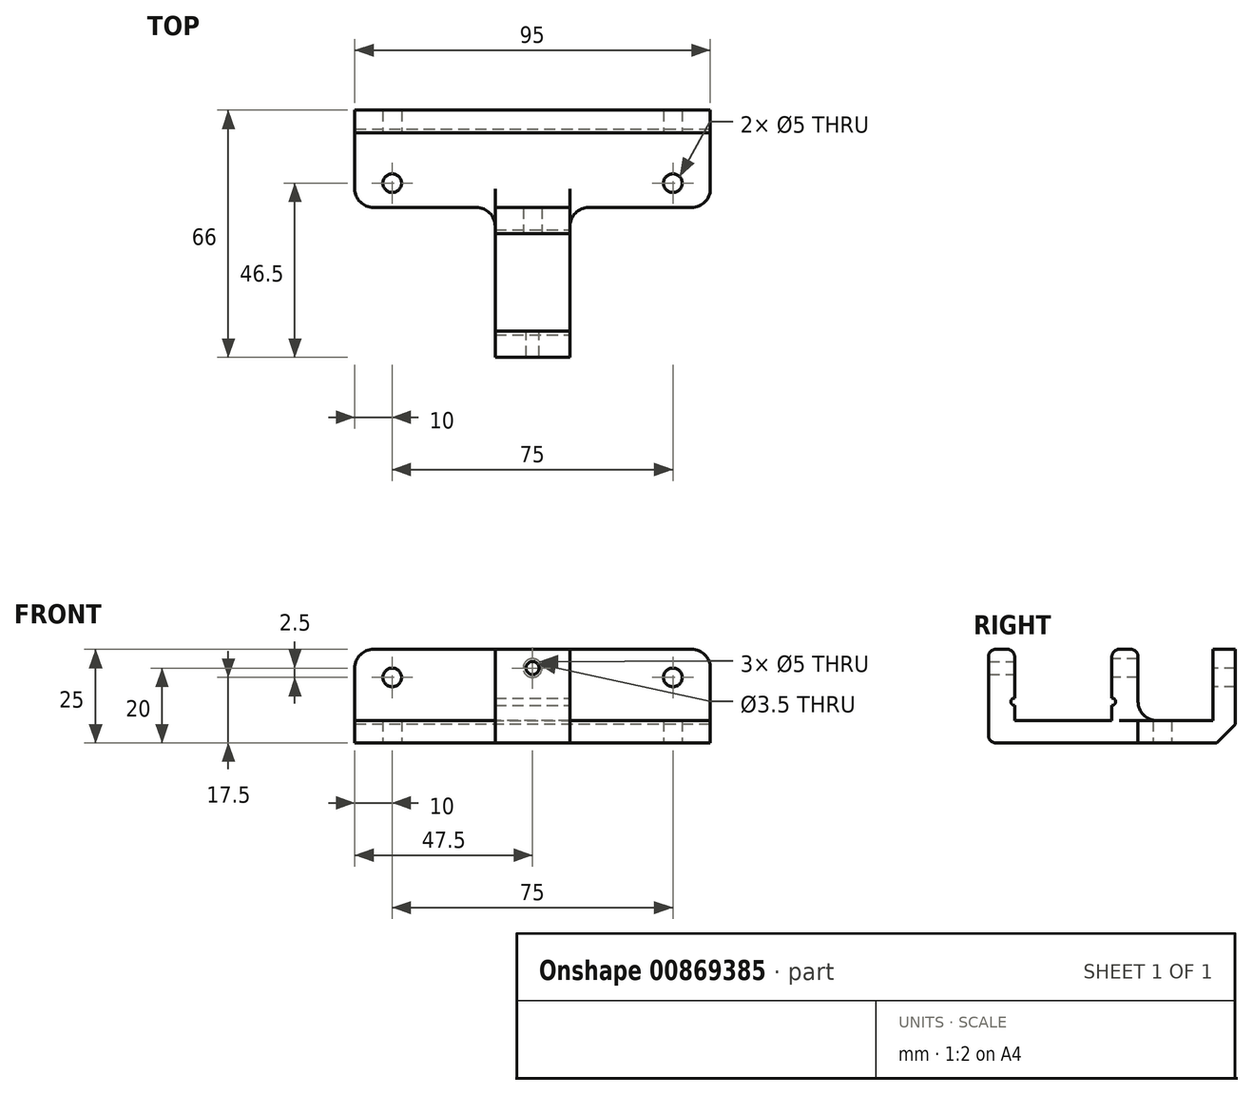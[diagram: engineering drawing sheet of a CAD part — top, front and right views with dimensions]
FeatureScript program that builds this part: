
annotation { "Feature Type Name" : "Feature", "Feature Type Description" : "" }
export const myFeature = defineFeature(function(context is Context, id is Id, definition is map)
    precondition{}
    {
        {
            var Q0;
            Q0=qCreatedBy(makeId("Top.planeOp"),FACE);
            var sketch = newSketch(context, id + "F0", { "sketchPlane" : qUnion([Q0])});
            skCircle(sketch, "E0", {"center": v(-37.5, 6.5) * mm, "radius": 2.5 * mm});
            skCircle(sketch, "E1", {"center": v(37.5, 6.5) * mm, "radius": 2.5 * mm});
            skLineSegment(sketch, "E2.bottom", {"start": v(-47.5, 0) * mm, "end": v(47.5, 0) * mm});
            skLineSegment(sketch, "E2.top", {"start": v(-47.5, 20) * mm, "end": v(47.5, 20) * mm});
            skLineSegment(sketch, "E2.left", {"start": v(-47.5, 0) * mm, "end": v(-47.5, 20) * mm});
            skLineSegment(sketch, "E2.right", {"start": v(47.5, 0) * mm, "end": v(47.5, 20) * mm});
            skLineSegment(sketch, "E3.top", {"start": v(-47.5, 26) * mm, "end": v(47.5, 26) * mm});
            skLineSegment(sketch, "E3.left", {"start": v(-47.5, 20) * mm, "end": v(-47.5, 26) * mm});
            skLineSegment(sketch, "E3.right", {"start": v(47.5, 20) * mm, "end": v(47.5, 26) * mm});
            skLineSegment(sketch, "E4.bottom", {"start": v(-10, 0) * mm, "end": v(10, 0) * mm});
            skLineSegment(sketch, "E4.top", {"start": v(-10, -40) * mm, "end": v(10, -40) * mm});
            skLineSegment(sketch, "E4.left", {"start": v(-10, 0) * mm, "end": v(-10, -40) * mm});
            skLineSegment(sketch, "E4.right", {"start": v(10, 0) * mm, "end": v(10, -40) * mm});
            skLineSegment(sketch, "E5.top", {"start": v(-10, -33) * mm, "end": v(10, -33) * mm});
            skLineSegment(sketch, "E5.left", {"start": v(-10, -40) * mm, "end": v(-10, -33) * mm});
            skLineSegment(sketch, "E5.right", {"start": v(10, -40) * mm, "end": v(10, -33) * mm});
            skLineSegment(sketch, "E6.top", {"start": v(-10, -7) * mm, "end": v(10, -7) * mm});
            skLineSegment(sketch, "E6.left", {"start": v(-10, 0) * mm, "end": v(-10, -7) * mm});
            skLineSegment(sketch, "E6.right", {"start": v(10, 0) * mm, "end": v(10, -7) * mm});
            skSolve(sketch);
        }
        {
            var Q0;
            Q0=makeQuery(id+"F0.imprint","IMPRINT",FACE,{"disambiguationData":[TD([[makeQuery(id+"F0.imprint","IMPRINT",EDGE,{"derivedFrom":sQuery(id+"F0.wireOp",EDGE,"E0")}),-1.0]])]});
            var Q1;
            {var subQ2=sQuery(id+"F0.wireOp",EDGE,"E5.top");Q1=makeQuery(id+"F0.imprint","IMPRINT",FACE,{"disambiguationData":[TD([[makeQuery(id+"F0.imprint","IMPRINT",EDGE,{"derivedFrom":subQ2}),1.0]])]});}
            var Q2;
            {var subQ0=sQuery(id+"F0.wireOp",EDGE,"E4.top");Q2=makeQuery(id+"F0.imprint","IMPRINT",FACE,{"disambiguationData":[TD([[makeQuery(id+"F0.imprint","IMPRINT",EDGE,{"derivedFrom":subQ0}),1.0]])]});}
            var Q3;
            {var subQ5=sQuery(id+"F0.wireOp",EDGE,"E6.top");Q3=makeQuery(id+"F0.imprint","IMPRINT",FACE,{"disambiguationData":[TD([[makeQuery(id+"F0.imprint","IMPRINT",EDGE,{"derivedFrom":subQ5}),1.0]])]});}
            extrude(context, id + "F1", {"entities" : qUnion([Q0, Q1, Q2, Q3]), "depth" : 6 * mm, "offsetDistance" : 25 * mm});
        }
        {
            var Q0;
            Q0=makeQuery(id+"F0.imprint","IMPRINT",FACE,{"disambiguationData":[TD([[makeQuery(id+"F0.imprint","IMPRINT",EDGE,{"derivedFrom":sQuery(id+"F0.wireOp",EDGE,"E2.top")}),1.0]])]});
            extrude(context, id + "F2", {"entities" : qUnion([Q0]), "operationType" : NewBodyOperationType.ADD, "depth" : 25 * mm, "offsetDistance" : 25 * mm});
        }
        {
            var Q0;
            Q0=makeQuery(id+"F2.opExtrude","SWEPT_FACE",FACE,{"disambiguationData":[OSD([sQuery(id+"F0.wireOp",EDGE,"E2.top")])]});
            var sketch = newSketch(context, id + "F3", { "sketchPlane" : qUnion([Q0])});
            skCircle(sketch, "E7", {"center": v(-37.5, 17.5) * mm, "radius": 2.5 * mm});
            skCircle(sketch, "E8", {"center": v(37.5, 17.5) * mm, "radius": 2.5 * mm});
            skSolve(sketch);
        }
        {
            var Q0;
            Q0=makeQuery(id+"F3.imprint","IMPRINT",FACE,{"disambiguationData":[TD([[makeQuery(id+"F3.imprint","IMPRINT",EDGE,{"derivedFrom":sQuery(id+"F3.wireOp",EDGE,"E7")}),1.0]])]});
            var Q1;
            Q1=makeQuery(id+"F3.imprint","IMPRINT",FACE,{"disambiguationData":[TD([[makeQuery(id+"F3.imprint","IMPRINT",EDGE,{"derivedFrom":sQuery(id+"F3.wireOp",EDGE,"E8")}),1.0]])]});
            extrude(context, id + "F4", {"entities" : qUnion([Q0, Q1]), "operationType" : NewBodyOperationType.REMOVE, "oppositeDirection" : true, "depth" : 25 * mm, "offsetDistance" : 25 * mm});
        }
        {
            var Q0;
            Q0=makeQuery(id+"F1.opExtrude","CAP_EDGE",EDGE,{"disambiguationData":[OSD([sQuery(id+"F0.wireOp",EDGE,"E2.top")])],"isStart":false});
            var Q1;
            Q1=makeQuery(id+"F2.opExtrude","CAP_EDGE",EDGE,{"disambiguationData":[OSD([sQuery(id+"F0.wireOp",EDGE,"E3.top")])],"isStart":true});
            chamfer(context, id + "F5", {"entities" : qUnion([Q0, Q1]), "width" : 5 * mm, "tangentPropagation" : true});
        }
        {
            var Q0;
            Q0=makeQuery(id+"F2.opExtrude","CAP_EDGE",EDGE,{"disambiguationData":[OSD([sQuery(id+"F0.wireOp",EDGE,"E3.right")])],"isStart":false});
            var Q1;
            Q1=makeQuery(id+"F1.opExtrude","SWEPT_EDGE",EDGE,{"disambiguationData":[OSD([sQuery(id+"F0.wireOp",EDGE,"E2.bottom"),sQuery(id+"F0.wireOp",EDGE,"E2.right")])]});
            var Q2;
            Q2=makeQuery(id+"F1.opExtrude","SWEPT_EDGE",EDGE,{"disambiguationData":[OSD([sQuery(id+"F0.wireOp",EDGE,"E2.bottom"),sQuery(id+"F0.wireOp",EDGE,"E2.left")])]});
            var Q3;
            Q3=makeQuery(id+"F2.opExtrude","CAP_EDGE",EDGE,{"disambiguationData":[OSD([sQuery(id+"F0.wireOp",EDGE,"E3.left")])],"isStart":false});
            fillet(context, id + "F6", {"entities" : qUnion([Q0, Q1, Q2, Q3]), "radius" : 5 * mm, "tangentPropagation" : true, "allowEdgeOverflow" : false});
        }
        {
            var Q0;
            {var subQ5=sQuery(id+"F0.wireOp",EDGE,"E6.top");Q0=makeQuery(id+"F0.imprint","IMPRINT",FACE,{"disambiguationData":[TD([[makeQuery(id+"F0.imprint","IMPRINT",EDGE,{"derivedFrom":subQ5}),1.0]])]});}
            var Q1;
            {var subQ0=sQuery(id+"F0.wireOp",EDGE,"E4.top");Q1=makeQuery(id+"F0.imprint","IMPRINT",FACE,{"disambiguationData":[TD([[makeQuery(id+"F0.imprint","IMPRINT",EDGE,{"derivedFrom":subQ0}),1.0]])]});}
            extrude(context, id + "F7", {"entities" : qUnion([Q0, Q1]), "operationType" : NewBodyOperationType.ADD, "depth" : 25 * mm, "offsetDistance" : 25 * mm});
        }
        {
            var Q0;
            {var subQ0=sQuery(id+"F0.wireOp",EDGE,"E4.right");Q0=makeQuery(id+"F7.boolean.opBoolean","MERGE",FACE,{"derivedFrom":[makeQuery(id+"F1.opExtrude","SWEPT_FACE",FACE,{"disambiguationData":[OSD([subQ0])]}),makeQuery(id+"F7.opExtrude","SWEPT_FACE",FACE,{"disambiguationData":[OSD([subQ0]),TDD([makeQuery(id+"F0.imprint","IMPRINT",EDGE,{"disambiguationData":[TD([[makeQuery(id+"F0.imprint","INTERSECT",VERTEX,{"derivedFrom":[sQuery(id+"F0.wireOp",EDGE,"E4.top"),subQ0]}),1.0]])],"derivedFrom":subQ0})])]}),makeQuery(id+"F7.opExtrude","SWEPT_FACE",FACE,{"disambiguationData":[OSD([subQ0]),TDD([makeQuery(id+"F0.imprint","IMPRINT",EDGE,{"disambiguationData":[TD([[makeQuery(id+"F0.imprint","INTERSECT",VERTEX,{"derivedFrom":[sQuery(id+"F0.wireOp",EDGE,"E2.bottom"),subQ0]}),-1.0]])],"derivedFrom":subQ0})])]})]});}
            var sketch = newSketch(context, id + "F8", { "sketchPlane" : qUnion([Q0])});
            skCircle(sketch, "E9", {"center": v(-33, 11) * mm, "radius": 1 * mm});
            skCircle(sketch, "E10", {"center": v(-7, 11) * mm, "radius": 1 * mm});
            skSolve(sketch);
        }
        {
            var Q0;
            {var subQ0=sQuery(id+"F8.wireOp",EDGE,"E9");var subQ1=makeQuery(id+"F7.opExtrude","SWEPT_EDGE",EDGE,{"disambiguationData":[OSD([sQuery(id+"F0.wireOp",EDGE,"E4.right"),sQuery(id+"F0.wireOp",EDGE,"E5.top")])]});var subQ2=makeQuery(id+"F8.imprint","INTERSECT",VERTEX,{"disambiguationData":[OD(0.0)],"derivedFrom":[subQ1,subQ0]});Q0=makeQuery(id+"F8.imprint","IMPRINT",FACE,{"disambiguationData":[TD([[makeQuery(id+"F8.imprint","IMPRINT",EDGE,{"disambiguationData":[TD([[subQ2,-1.0]])],"derivedFrom":subQ0}),1.0]])]});}
            var Q1;
            {var subQ0=sQuery(id+"F8.wireOp",EDGE,"E10");var subQ1=makeQuery(id+"F7.opExtrude","SWEPT_EDGE",EDGE,{"disambiguationData":[OSD([sQuery(id+"F0.wireOp",EDGE,"E4.right"),sQuery(id+"F0.wireOp",EDGE,"E6.top")])]});var subQ2=makeQuery(id+"F8.imprint","INTERSECT",VERTEX,{"disambiguationData":[OD(0.0)],"derivedFrom":[subQ1,subQ0]});Q1=makeQuery(id+"F8.imprint","IMPRINT",FACE,{"disambiguationData":[TD([[makeQuery(id+"F8.imprint","IMPRINT",EDGE,{"disambiguationData":[TD([[subQ2,1.0]])],"derivedFrom":subQ0}),1.0]])]});}
            extrude(context, id + "F9", {"entities" : qUnion([Q0, Q1]), "operationType" : NewBodyOperationType.REMOVE, "oppositeDirection" : true, "depth" : 25 * mm, "offsetDistance" : 25 * mm});
        }
        {
            var Q0;
            {var subQ0=sQuery(id+"F0.wireOp",EDGE,"E6.top");var subQ1=sQuery(id+"F0.wireOp",EDGE,"E4.right");var subQ2=sQuery(id+"F0.wireOp",EDGE,"E4.left");var subQ3=sQuery(id+"F0.wireOp",EDGE,"E2.bottom");Q0=makeQuery(id+"F9.boolean.opBoolean","SPLIT",FACE,{"disambiguationData":[TD([makeQuery(id+"F7.opExtrude","CAP_FACE",FACE,{"disambiguationData":[OSD([subQ3,subQ2,subQ1,subQ0])],"isStart":false})])],"derivedFrom":makeQuery(id+"F7.opExtrude","SWEPT_FACE",FACE,{"disambiguationData":[OSD([subQ0])]})});}
            var sketch = newSketch(context, id + "F10", { "sketchPlane" : qUnion([Q0])});
            skCircle(sketch, "E11", {"center": v(0, 20) * mm, "radius": 1.75 * mm});
            skPoint(sketch, "E11.centerSnap0", {"position": v(0, 25) * mm});
            skCircle(sketch, "E12", {"center": v(0, 20) * mm, "radius": 2.5 * mm});
            skSolve(sketch);
        }
        {
            var Q0;
            Q0=makeQuery(id+"F10.imprint","IMPRINT",FACE,{"disambiguationData":[TD([[makeQuery(id+"F10.imprint","IMPRINT",EDGE,{"derivedFrom":sQuery(id+"F10.wireOp",EDGE,"E11")}),1.0]])]});
            extrude(context, id + "F11", {"entities" : qUnion([Q0]), "operationType" : NewBodyOperationType.REMOVE, "depth" : 50 * mm, "offsetDistance" : 25 * mm});
        }
        {
            var Q0;
            Q0=makeQuery(id+"F10.imprint","IMPRINT",FACE,{"disambiguationData":[TD([[makeQuery(id+"F10.imprint","IMPRINT",EDGE,{"derivedFrom":sQuery(id+"F10.wireOp",EDGE,"E11")}),-1.0]])]});
            var Q1;
            Q1=makeQuery(id+"F10.imprint","IMPRINT",FACE,{"disambiguationData":[TD([[makeQuery(id+"F10.imprint","IMPRINT",EDGE,{"derivedFrom":sQuery(id+"F10.wireOp",EDGE,"E11")}),1.0]])]});
            extrude(context, id + "F12", {"entities" : qUnion([Q0, Q1]), "operationType" : NewBodyOperationType.REMOVE, "oppositeDirection" : true, "depth" : 10 * mm, "offsetDistance" : 25 * mm});
        }
        {
            var Q0;
            Q0=makeQuery(id+"F7.opExtrude","CAP_EDGE",EDGE,{"disambiguationData":[OSD([sQuery(id+"F0.wireOp",EDGE,"E6.top")])],"isStart":false});
            var Q1;
            Q1=makeQuery(id+"F7.opExtrude","CAP_EDGE",EDGE,{"disambiguationData":[OSD([sQuery(id+"F0.wireOp",EDGE,"E2.bottom")])],"isStart":false});
            var Q2;
            Q2=makeQuery(id+"F7.opExtrude","CAP_EDGE",EDGE,{"disambiguationData":[OSD([sQuery(id+"F0.wireOp",EDGE,"E5.top")])],"isStart":false});
            var Q3;
            Q3=makeQuery(id+"F7.opExtrude","CAP_EDGE",EDGE,{"disambiguationData":[OSD([sQuery(id+"F0.wireOp",EDGE,"E4.top")])],"isStart":false});
            var Q4;
            Q4=makeQuery(id+"F1.opExtrude","CAP_EDGE",EDGE,{"disambiguationData":[OSD([sQuery(id+"F0.wireOp",EDGE,"E4.top")])],"isStart":true});
            fillet(context, id + "F13", {"entities" : qUnion([Q0, Q1, Q2, Q3, Q4]), "radius" : 2 * mm, "tangentPropagation" : true, "allowEdgeOverflow" : false});
        }
        {
            var Q0;
            {var subQ0=sQuery(id+"F0.wireOp",EDGE,"E2.bottom");Q0=makeQuery(id+"F7.boolean.opBoolean","INTERSECT",EDGE,{"derivedFrom":[makeQuery(id+"F1.opExtrude","CAP_FACE",FACE,{"disambiguationData":[OSD([sQuery(id+"F0.wireOp",EDGE,"E0"),sQuery(id+"F0.wireOp",EDGE,"E1"),subQ0,sQuery(id+"F0.wireOp",EDGE,"E2.top"),sQuery(id+"F0.wireOp",EDGE,"E2.left"),sQuery(id+"F0.wireOp",EDGE,"E2.right"),sQuery(id+"F0.wireOp",EDGE,"E4.top"),sQuery(id+"F0.wireOp",EDGE,"E4.left"),sQuery(id+"F0.wireOp",EDGE,"E4.right")])],"isStart":false}),makeQuery(id+"F7.opExtrude","SWEPT_FACE",FACE,{"disambiguationData":[OSD([subQ0])]})]});}
            fillet(context, id + "F14", {"entities" : qUnion([Q0]), "radius" : 5 * mm, "tangentPropagation" : true, "allowEdgeOverflow" : false});
        }
        {
            var Q0;
            Q0=makeQuery(id+"F1.opExtrude","SWEPT_EDGE",EDGE,{"disambiguationData":[OSD([sQuery(id+"F0.wireOp",EDGE,"E2.bottom"),sQuery(id+"F0.wireOp",EDGE,"E4.right")])]});
            var Q1;
            Q1=makeQuery(id+"F1.opExtrude","SWEPT_EDGE",EDGE,{"disambiguationData":[OSD([sQuery(id+"F0.wireOp",EDGE,"E2.bottom"),sQuery(id+"F0.wireOp",EDGE,"E4.left")])]});
            fillet(context, id + "F15", {"entities" : qUnion([Q0, Q1]), "radius" : 5 * mm, "tangentPropagation" : true, "allowEdgeOverflow" : false});
        }
    });
